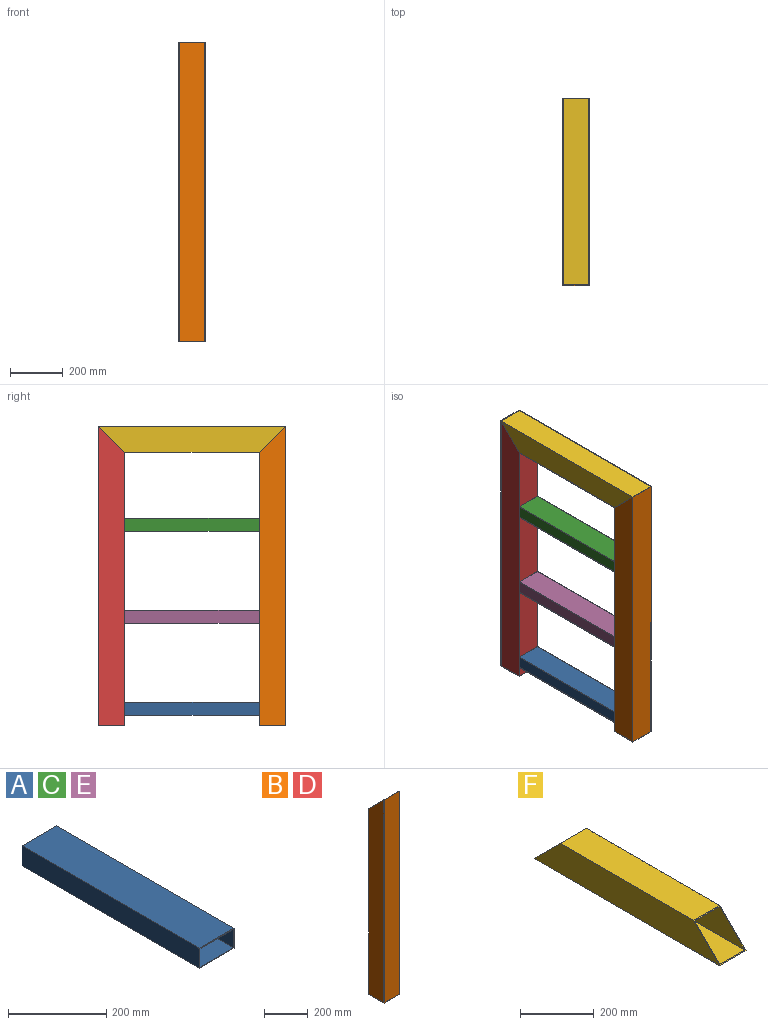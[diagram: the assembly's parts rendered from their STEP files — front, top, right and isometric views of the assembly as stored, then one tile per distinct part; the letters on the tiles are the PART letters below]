
ASSEMBLY  parts=6 mates=2
PART A: 10 faces, bbox 100x511x50 mm
  f0: plane 511x100mm, normal (0,0,1), area 51100mm2, adj f1,f7,f8,f9
  f1: plane 511x50mm, normal (-1,0,0), area 25550mm2, adj f0,f2,f8,f9
  f2: plane 511x100mm, normal (0,0,-1), area 51100mm2, adj f1,f7,f8,f9
  f3: plane 511x46mm, normal (1,0,0), area 23506mm2, adj f4,f6,f8,f9
  f4: plane 511x96mm, normal (0,0,-1), area 49056mm2, adj f3,f5,f8,f9
  f5: plane 511x46mm, normal (-1,0,0), area 23506mm2, adj f4,f6,f8,f9
  f6: plane 511x96mm, normal (0,0,1), area 49056mm2, adj f3,f5,f8,f9
  f7: plane 511x50mm, normal (1,0,0), area 25550mm2, adj f0,f2,f8,f9
  f8: plane 100x50mm, normal (0,-1,0), area 584mm2, adj f0,f1,f2,f3,f4,f5,f6,f7
  f9: plane 100x50mm, normal (0,1,0), area 584mm2, adj f0,f1,f2,f3,f4,f5,f6,f7
PART B: 10 faces, bbox 100x100x1140 mm
  f0: plane 1040x100mm, normal (0,1,0), area 104000mm2, adj f1,f7,f8,f9
  f1: plane 1140x100mm, normal (-1,0,0), area 109000mm2, adj f0,f2,f8,f9
  f2: plane 1140x100mm, normal (0,-1,0), area 114000mm2, adj f1,f7,f8,f9
  f3: plane 1138x96mm, normal (1,0,0), area 104640mm2, adj f4,f6,f8,f9
  f4: plane 1042x96.96mm, normal (0,-1,0), area 101032.3mm2, adj f3,f5,f8,f9
  f5: plane 1138x96mm, normal (-1,0,0), area 104640mm2, adj f4,f6,f8,f9
  f6: plane 1138x96.96mm, normal (0,1,0), area 110340.5mm2, adj f3,f5,f8,f9
  f7: plane 1140x100mm, normal (1,0,0), area 109000mm2, adj f0,f2,f8,f9
  f8: plane 100x100mm, normal (0,0,-1), area 691.8mm2, adj f0,f1,f2,f3,f4,f5,f6,f7
  f9: plane 100x100mm, normal (0,0.71,0.71), area 978.4mm2, adj f0,f1,f2,f3,f4,f5,f6,f7
PART C: same geometry as A
PART D: same geometry as B
PART E: same geometry as A
PART F: 10 faces, bbox 100x711x100 mm
  f0: plane 511x100mm, normal (0,0,1), area 51100mm2, adj f1,f7,f8,f9
  f1: plane 711x100mm, normal (-1,0,0), area 61100mm2, adj f0,f2,f8,f9
  f2: plane 711x100mm, normal (0,0,-1), area 71100mm2, adj f1,f7,f8,f9
  f3: plane 707x96mm, normal (1,0,0), area 58656mm2, adj f4,f6,f8,f9
  f4: plane 515x96mm, normal (0,0,-1), area 49440mm2, adj f3,f5,f8,f9
  f5: plane 707x96mm, normal (-1,0,0), area 58656mm2, adj f4,f6,f8,f9
  f6: plane 707x96mm, normal (0,0,1), area 67872mm2, adj f3,f5,f8,f9
  f7: plane 711x100mm, normal (1,0,0), area 61100mm2, adj f0,f2,f8,f9
  f8: plane 100x100mm, normal (0,-0.71,0.71), area 1108.7mm2, adj f0,f1,f2,f3,f4,f5,f6,f7
  f9: plane 100x100mm, normal (0,0.71,0.71), area 1108.7mm2, adj f0,f1,f2,f3,f4,f5,f6,f7
PLACE A t=(590.81,605.37,121.59)mm
PLACE B t=(469.93,44.37,-452.12)mm
PLACE C t=(590.73,605.58,821.59)mm
PLACE D rot(axis=(0,0,1),180deg) t=(469.93,655.37,-452.12)mm
PLACE E t=(590.68,605.7,471.59)mm
PLACE F rot(axis=(0,1,0),180deg) t=(1031.76,705.37,637.88)mm
MATE fastened D.f9 <-> F.f9  axis (0,-0.71,0.71) through (469.93,705.37,687.88)mm
MATE fastened F.f8 <-> B.f9  axis (0,-0.71,-0.71) through (469.93,-5.63,687.88)mm
